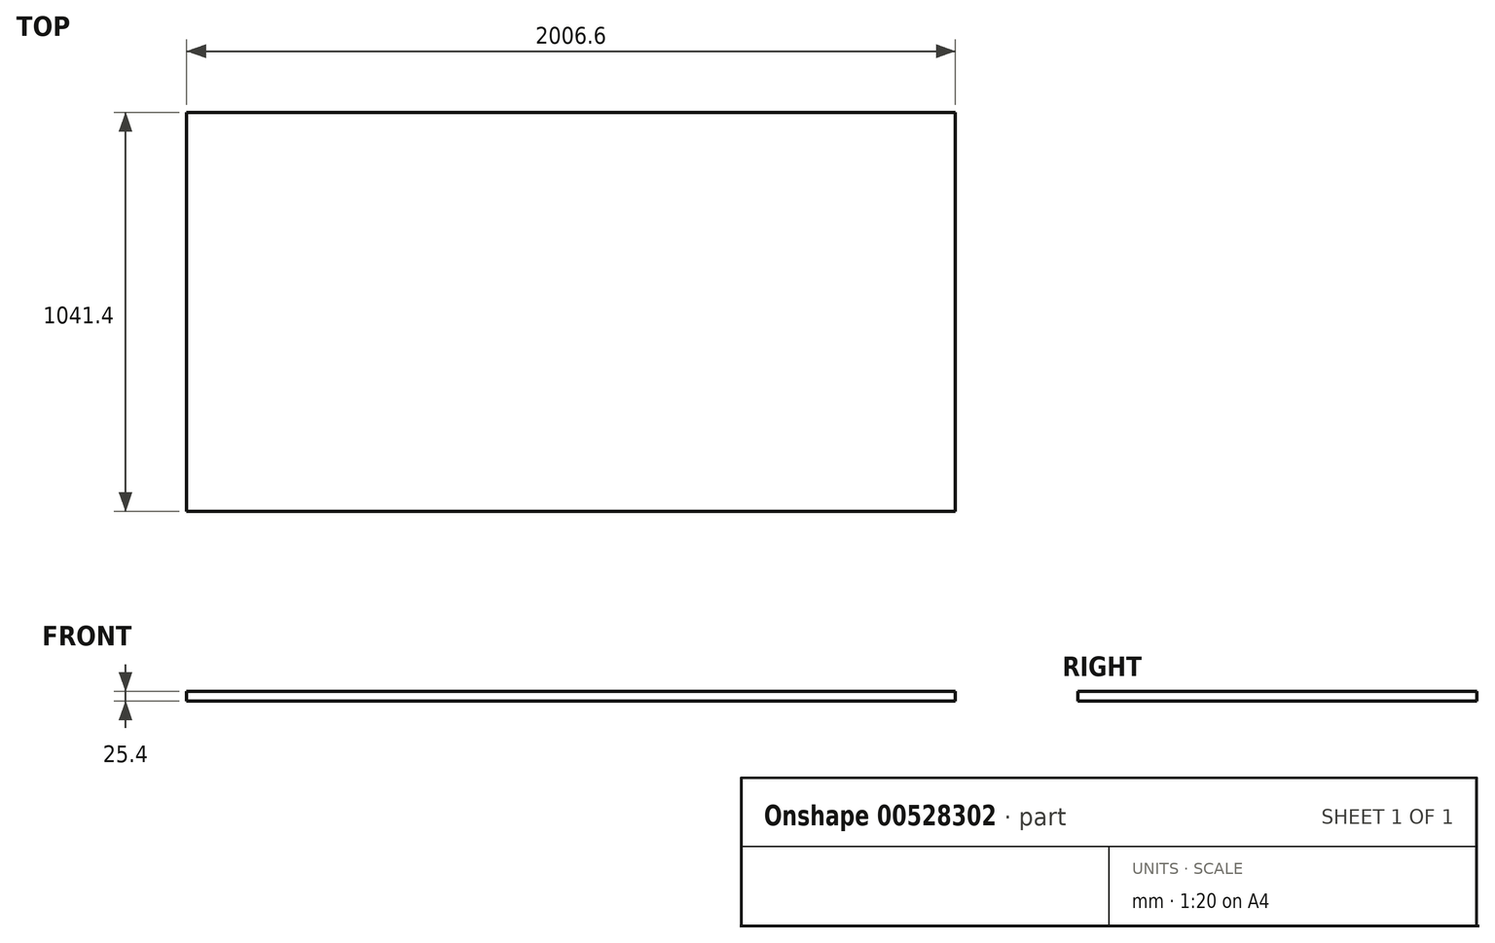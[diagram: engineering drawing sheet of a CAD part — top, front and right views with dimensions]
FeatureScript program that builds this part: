
annotation { "Feature Type Name" : "Feature", "Feature Type Description" : "" }
export const myFeature = defineFeature(function(context is Context, id is Id, definition is map)
    precondition{}
    {
        {
            var Q0;
            Q0=qCreatedBy(makeId("Top.planeOp"),FACE);
            var sketch = newSketch(context, id + "F0", { "sketchPlane" : qUnion([Q0])});
            skLineSegment(sketch, "E0.bottom", {"start": v(1003.3, -520.7) * mm, "end": v(-1003.3, -520.7) * mm});
            skLineSegment(sketch, "E0.top", {"start": v(1003.3, 520.7) * mm, "end": v(-1003.3, 520.7) * mm});
            skLineSegment(sketch, "E0.left", {"start": v(1003.3, -520.7) * mm, "end": v(1003.3, 520.7) * mm});
            skLineSegment(sketch, "E0.right", {"start": v(-1003.3, -520.7) * mm, "end": v(-1003.3, 520.7) * mm});
            skPoint(sketch, "E0.middle", {"position": v(0, 0) * mm});
            skSolve(sketch);
        }
        {
            var Q0;
            Q0=makeQuery(id+"F0.imprint","IMPRINT",FACE,{"disambiguationData":[TD([[makeQuery(id+"F0.imprint","IMPRINT",EDGE,{"derivedFrom":sQuery(id+"F0.wireOp",EDGE,"E0.bottom")}),-1.0]])]});
            extrude(context, id + "F1", {"entities" : qUnion([Q0]), "depth" : 25.4 * mm, "offsetDistance" : 25.4 * mm});
        }
    });
